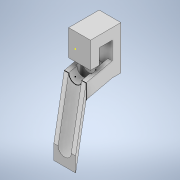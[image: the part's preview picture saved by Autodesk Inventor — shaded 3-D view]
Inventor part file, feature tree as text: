
AUTODESK INVENTOR PART (.ipt)
format: ipt  version: 2021 (Build 250183000, 183)  size: 443,392 bytes
history: native  units: mm
features: sketch x13, extrude x6, plane x3, sweep x1, thread x1, loft x1, emboss x1, other x1
ambient origin geometry x8: Origin, YZ Plane, XZ Plane, XY Plane, X Axis, Y Axis, Z Axis, Center Point
bodies: Solid1 (feature_tree)
feature tree (27):
  extrude  "Extrusion1"  Depth=50.0mm
  extrude  "Extrusion2"  Depth=12.5mm
  extrude  "Extrusion3"  Depth=3.0mm
  extrude  "Extrusion4"  Depth=6.0mm TaperAngle=0.0deg
  extrude  "Extrusion5"  Depth=15.0mm TaperAngle=0.0deg
  sketch  "Sketch6"  dims[d14=25.0mm d15=10.0mm d16=0.0mm d17=15.0mm]
  plane  "Work Plane1"
  sweep  "Sweep1"
  thread  "Thread1"  [1 undecoded]
  sketch  "Sketch9"  dims[d21=30.0mm d22=15.0mm]
  sketch  "Sketch10"  dims[d23=17.0mm]
  plane  "Work Plane2"
  extrude  "Extrusion6"  Depth=10.0mm TaperAngle=0.0deg
  sketch  "Sketch13"  dims[d25=-12.5mm]
  plane  "Work Plane3"
  loft  "Loft1"
  emboss  "Emboss1"
  sketch  "Sketch1"  dims[d0=25.0mm d1=50.0mm]
  sketch  "Sketch2"  dims[d2=12.5mm d3=12.5mm]
  sketch  "Sketch3"  dims[d4=10.0mm d5=0.0mm d7=3.0mm]
  sketch  "Sketch4"  dims[d8=33.0mm d9=6.0mm d10=0.0mm]
  sketch  "Sketch5"  dims[d11=15.0mm d12=15.0mm d13=0.0mm]
  sketch  "Sketch8"  dims[d18=15.0mm d19=10.0mm d20=0.0mm]
  sketch  "Sketch12"  dims[d24=17.0mm]
  sketch  "Sketch14"  dims[d26=2.268928mm]
  other  "Edges1"
  sketch  "Sketch15"  dims[d27=8.5mm d28=0.0mm d29=0.0mm d30=6.0mm d31=0.0mm d32=30.0mm d33=18.0mm d34=6.0mm d35=3.5mm d36=14.5mm d37=25.0mm d38=0.0mm d39=40.0mm d40=17.0mm d41=25.0mm d42=5.0mm d43=5.0mm d45=15.0mm d46=38.574mm d47=28.0mm d48=0.0mm d49=90.0deg d50=0.0mm d51=90.0deg d52=1.0mm d53=0.0mm]
note: 1 required parameter value undecoded (feature->parameter linkage not recoverable at this tier; creation-order binding heuristic only, values carry confidence <= 0.55)
